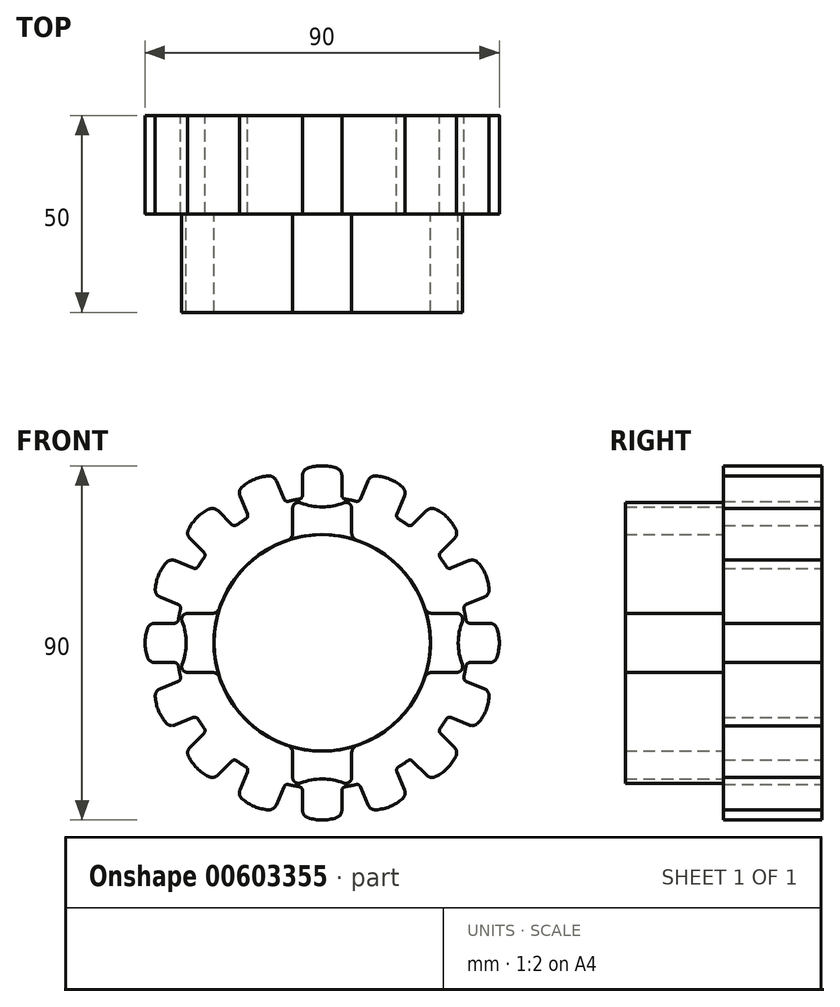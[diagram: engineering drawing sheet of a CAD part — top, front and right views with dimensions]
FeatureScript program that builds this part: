
annotation { "Feature Type Name" : "Feature", "Feature Type Description" : "" }
export const myFeature = defineFeature(function(context is Context, id is Id, definition is map)
    precondition{}
    {
        {
            var Q0;
            Q0=qCreatedBy(makeId("Front.planeOp"),FACE);
            var sketch = newSketch(context, id + "F0", { "sketchPlane" : qUnion([Q0])});
            skCircle(sketch, "E0", {"center": v(0, 0) * mm, "radius": 45 * mm});
            skCircle(sketch, "E1", {"center": v(0, 0) * mm, "radius": 37 * mm});
            skLineSegment(sketch, "E2", {"start": v(0, 0) * mm, "end": v(0, 45) * mm, "construction": true});
            skLineSegment(sketch, "E3", {"start": v(-5, 43.83) * mm, "end": v(-5, 36.66) * mm});
            skLineSegment(sketch, "E4.MirrorCS", {"start": v(5, 43.83) * mm, "end": v(5, 36.66) * mm});
            skArc(sketch, "E5.trimOffspring", {"start": v(5, 43.83) * mm, "mid": v(0, 45) * mm, "end": v(-5, 43.83) * mm});
            skSolve(sketch);
        }
        {
            var Q0;
            Q0=qCreatedBy(makeId("Right.planeOp"),FACE);
            var sketch = newSketch(context, id + "F1", { "sketchPlane" : qUnion([Q0])});
            skLineSegment(sketch, "E6", {"start": v(0, 0) * mm, "end": v(-32.43, 0) * mm, "construction": true});
            skSolve(sketch);
        }
        {
            var Q0;
            {var subQ0=sQuery(id+"F0.wireOp",EDGE,"E1");var subQ1=makeQuery(id+"F0.imprint","INTERSECT",VERTEX,{"derivedFrom":[subQ0,sQuery(id+"F0.wireOp",EDGE,"E3")]});Q0=makeQuery(id+"F0.imprint","IMPRINT",FACE,{"disambiguationData":[TD([[makeQuery(id+"F0.imprint","IMPRINT",EDGE,{"disambiguationData":[TD([[subQ1,1.0]])],"derivedFrom":subQ0}),1.0]])]});}
            var Q1;
            {var subQ3=sQuery(id+"F0.wireOp",EDGE,"E3");Q1=makeQuery(id+"F0.imprint","IMPRINT",FACE,{"disambiguationData":[TD([[makeQuery(id+"F0.imprint","IMPRINT",EDGE,{"derivedFrom":subQ3}),1.0]])]});}
            extrude(context, id + "F2", {"entities" : qUnion([Q0, Q1]), "depth" : 25 * mm, "offsetDistance" : 25 * mm});
        }
        {
            var Q0;
            Q0=makeQuery(id+"F2.opExtrude","SWEPT_EDGE",EDGE,{"disambiguationData":[OSD([sQuery(id+"F0.wireOp",EDGE,"E3"),sQuery(id+"F0.wireOp",EDGE,"E5.trimOffspring")])]});
            var Q1;
            Q1=makeQuery(id+"F2.opExtrude","SWEPT_EDGE",EDGE,{"disambiguationData":[OSD([sQuery(id+"F0.wireOp",EDGE,"E4.MirrorCS"),sQuery(id+"F0.wireOp",EDGE,"E5.trimOffspring")])]});
            fillet(context, id + "F3", {"entities" : qUnion([Q0, Q1]), "radius" : 2 * mm, "tangentPropagation" : true, "allowEdgeOverflow" : false});
        }
        {
            var Q0;
            Q0=makeQuery(id+"F2.opExtrude","SWEPT_EDGE",EDGE,{"disambiguationData":[OSD([sQuery(id+"F0.wireOp",EDGE,"E1"),sQuery(id+"F0.wireOp",EDGE,"E3")])]});
            var Q1;
            Q1=makeQuery(id+"F2.opExtrude","SWEPT_EDGE",EDGE,{"disambiguationData":[OSD([sQuery(id+"F0.wireOp",EDGE,"E1"),sQuery(id+"F0.wireOp",EDGE,"E4.MirrorCS")])]});
            fillet(context, id + "F4", {"entities" : qUnion([Q0, Q1]), "radius" : 1 * mm, "tangentPropagation" : true, "allowEdgeOverflow" : false});
        }
        {
            var Q0;
            Q0=makeQuery(id+"F2.opExtrude","SWEPT_BODY",BODY,{"disambiguationData":[OSD([sQuery(id+"F0.wireOp",EDGE,"E1"),sQuery(id+"F0.wireOp",EDGE,"E3"),sQuery(id+"F0.wireOp",EDGE,"E4.MirrorCS"),sQuery(id+"F0.wireOp",EDGE,"E5.trimOffspring")])]});
            var Q1;
            Q1=sQuery(id+"F1.wireOp",EDGE,"E6");
            circularPattern(context, id + "F5", {"operationType" : NewBodyOperationType.ADD, "entities" : qUnion([Q0]), "axis" : qUnion([Q1]), "angle" : 360 * degree, "instanceCount" : 16, "equalSpace" : true});
        }
        {
            var Q0;
            {var subQ0=makeQuery(id+"F2.opExtrude","CAP_FACE",FACE,{"disambiguationData":[OSD([sQuery(id+"F0.wireOp",EDGE,"E1"),sQuery(id+"F0.wireOp",EDGE,"E3"),sQuery(id+"F0.wireOp",EDGE,"E4.MirrorCS"),sQuery(id+"F0.wireOp",EDGE,"E5.trimOffspring")])],"isStart":false});Q0=makeQuery(id+"F5.boolean.opBoolean","MERGE",FACE,{"derivedFrom":[subQ0,makeQuery(id+"F5.opPattern","COPY",FACE,{"derivedFrom":subQ0,"instanceName":"1"}),makeQuery(id+"F5.opPattern","COPY",FACE,{"derivedFrom":subQ0,"instanceName":"2"}),makeQuery(id+"F5.opPattern","COPY",FACE,{"derivedFrom":subQ0,"instanceName":"3"}),makeQuery(id+"F5.opPattern","COPY",FACE,{"derivedFrom":subQ0,"instanceName":"4"}),makeQuery(id+"F5.opPattern","COPY",FACE,{"derivedFrom":subQ0,"instanceName":"5"}),makeQuery(id+"F5.opPattern","COPY",FACE,{"derivedFrom":subQ0,"instanceName":"6"}),makeQuery(id+"F5.opPattern","COPY",FACE,{"derivedFrom":subQ0,"instanceName":"7"}),makeQuery(id+"F5.opPattern","COPY",FACE,{"derivedFrom":subQ0,"instanceName":"8"}),makeQuery(id+"F5.opPattern","COPY",FACE,{"derivedFrom":subQ0,"instanceName":"9"}),makeQuery(id+"F5.opPattern","COPY",FACE,{"derivedFrom":subQ0,"instanceName":"10"}),makeQuery(id+"F5.opPattern","COPY",FACE,{"derivedFrom":subQ0,"instanceName":"11"}),makeQuery(id+"F5.opPattern","COPY",FACE,{"derivedFrom":subQ0,"instanceName":"12"}),makeQuery(id+"F5.opPattern","COPY",FACE,{"derivedFrom":subQ0,"instanceName":"13"}),makeQuery(id+"F5.opPattern","COPY",FACE,{"derivedFrom":subQ0,"instanceName":"14"}),makeQuery(id+"F5.opPattern","COPY",FACE,{"derivedFrom":subQ0,"instanceName":"15"})]});}
            var sketch = newSketch(context, id + "F6", { "sketchPlane" : qUnion([Q0])});
            skCircle(sketch, "E7", {"center": v(0, 0) * mm, "radius": 35 * mm, "construction": true});
            skCircle(sketch, "E8", {"center": v(0, 0) * mm, "radius": 27.5 * mm});
            skLineSegment(sketch, "E9", {"start": v(-7.5, 34.19) * mm, "end": v(-7.5, 26.46) * mm});
            skLineSegment(sketch, "E10", {"start": v(0, 0) * mm, "end": v(0, 36.97) * mm, "construction": true});
            skLineSegment(sketch, "E11.MirrorCS", {"start": v(7.5, 34.19) * mm, "end": v(7.5, 26.46) * mm});
            skArc(sketch, "E12", {"start": v(-5.45, 35.58) * mm, "mid": v(0, 34.56) * mm, "end": v(5.45, 35.58) * mm});
            skArc(sketch, "E13", {"start": v(-5.45, 35.58) * mm, "mid": v(-6.85, 35.43) * mm, "end": v(-7.5, 34.19) * mm});
            skArc(sketch, "E14.MirrorC", {"start": v(5.45, 35.58) * mm, "mid": v(6.85, 35.43) * mm, "end": v(7.5, 34.19) * mm});
            skSolve(sketch);
        }
        {
            var Q0;
            {var subQ1=sQuery(id+"F6.wireOp",EDGE,"E9");Q0=makeQuery(id+"F6.imprint","IMPRINT",FACE,{"disambiguationData":[TD([[makeQuery(id+"F6.imprint","IMPRINT",EDGE,{"derivedFrom":subQ1}),1.0]])]});}
            var Q1;
            {var subQ0=sQuery(id+"F6.wireOp",EDGE,"E8");var subQ1=makeQuery(id+"F6.imprint","INTERSECT",VERTEX,{"derivedFrom":[subQ0,sQuery(id+"F6.wireOp",EDGE,"E9")]});Q1=makeQuery(id+"F6.imprint","IMPRINT",FACE,{"disambiguationData":[TD([[makeQuery(id+"F6.imprint","IMPRINT",EDGE,{"disambiguationData":[TD([[subQ1,1.0]])],"derivedFrom":subQ0}),1.0]])]});}
            extrude(context, id + "F7", {"entities" : qUnion([Q0, Q1]), "operationType" : NewBodyOperationType.ADD, "depth" : 25 * mm, "offsetDistance" : 25 * mm});
        }
        {
            var Q0;
            Q0=makeQuery(id+"F7.opExtrude","SWEPT_EDGE",EDGE,{"disambiguationData":[OSD([sQuery(id+"F6.wireOp",EDGE,"E8"),sQuery(id+"F6.wireOp",EDGE,"E9")])]});
            var Q1;
            Q1=makeQuery(id+"F7.opExtrude","SWEPT_EDGE",EDGE,{"disambiguationData":[OSD([sQuery(id+"F6.wireOp",EDGE,"E8"),sQuery(id+"F6.wireOp",EDGE,"E11.MirrorCS")])]});
            fillet(context, id + "F8", {"entities" : qUnion([Q0, Q1]), "radius" : 2 * mm, "tangentPropagation" : true, "allowEdgeOverflow" : false});
        }
        {
            var Q0;
            Q0=makeQuery(id+"F2.opExtrude","SWEPT_BODY",BODY,{"disambiguationData":[OSD([sQuery(id+"F0.wireOp",EDGE,"E1"),sQuery(id+"F0.wireOp",EDGE,"E3"),sQuery(id+"F0.wireOp",EDGE,"E4.MirrorCS"),sQuery(id+"F0.wireOp",EDGE,"E5.trimOffspring")])]});
            var Q1;
            Q1=sQuery(id+"F1.wireOp",EDGE,"E6");
            circularPattern(context, id + "F9", {"entities" : qUnion([Q0]), "axis" : qUnion([Q1]), "angle" : 360 * degree, "instanceCount" : 4, "equalSpace" : true});
        }
    });
